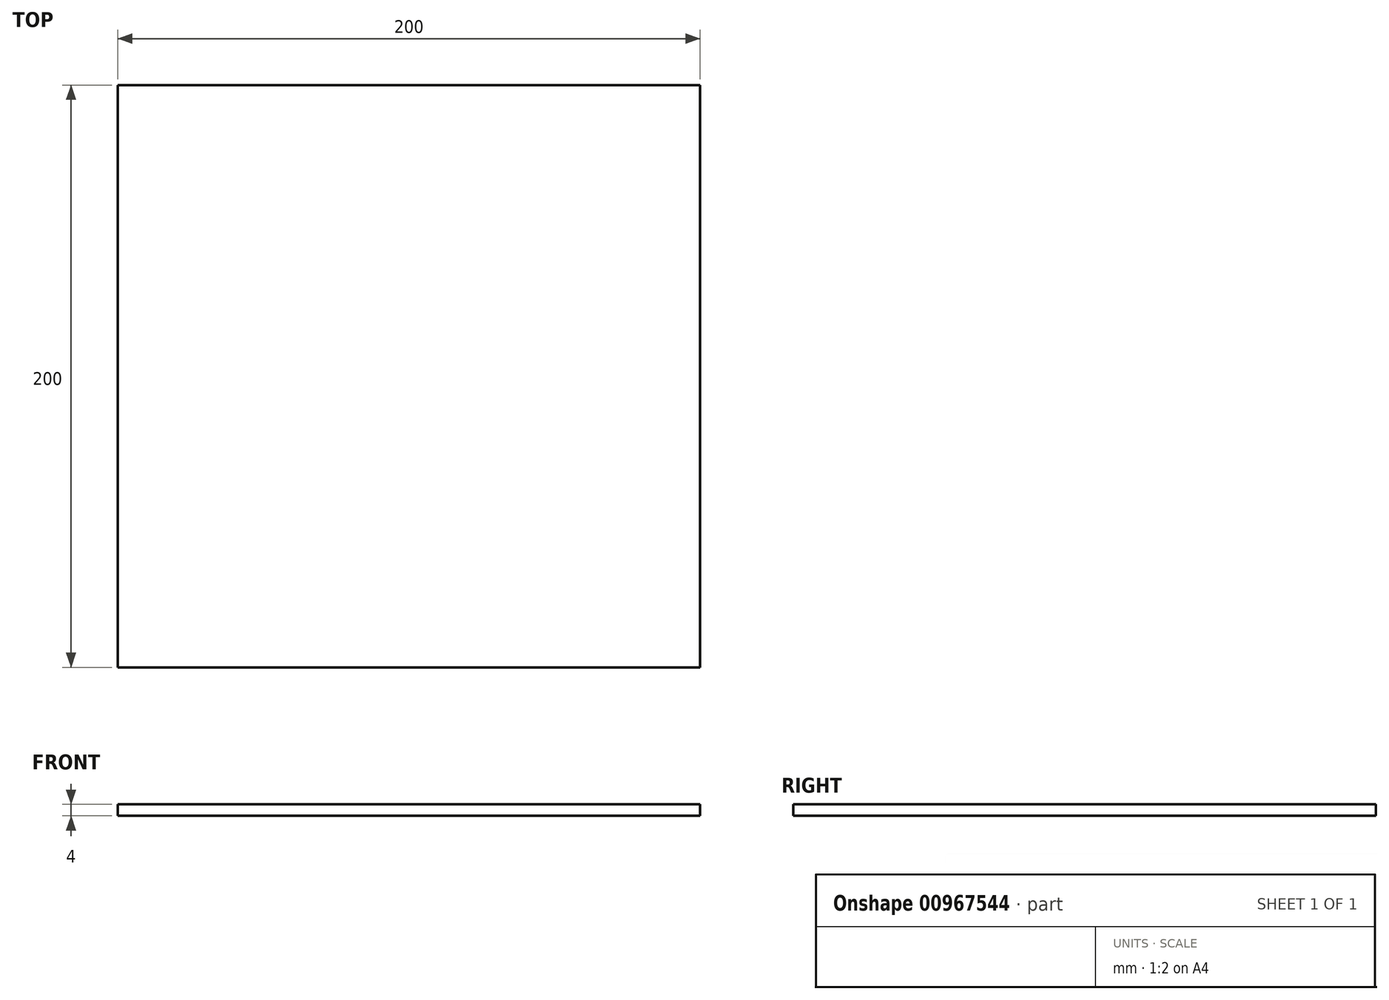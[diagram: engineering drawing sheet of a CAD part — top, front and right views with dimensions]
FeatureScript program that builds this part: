
annotation { "Feature Type Name" : "Feature", "Feature Type Description" : "" }
export const myFeature = defineFeature(function(context is Context, id is Id, definition is map)
    precondition{}
    {
        {
            var Q0;
            Q0=qCreatedBy(makeId("Top.planeOp"),FACE);
            var sketch = newSketch(context, id + "F0", { "sketchPlane" : qUnion([Q0])});
            skLineSegment(sketch, "E0.bottom", {"start": v(100, -100) * mm, "end": v(-100, -100) * mm});
            skLineSegment(sketch, "E0.top", {"start": v(100, 100) * mm, "end": v(-100, 100) * mm});
            skLineSegment(sketch, "E0.left", {"start": v(100, -100) * mm, "end": v(100, 100) * mm});
            skLineSegment(sketch, "E0.right", {"start": v(-100, -100) * mm, "end": v(-100, 100) * mm});
            skPoint(sketch, "E0.middle", {"position": v(0, 0) * mm});
            skSolve(sketch);
        }
        {
            var Q0;
            Q0=makeQuery(id+"F0.imprint","IMPRINT",FACE,{"disambiguationData":[TD([[makeQuery(id+"F0.imprint","IMPRINT",EDGE,{"derivedFrom":sQuery(id+"F0.wireOp",EDGE,"E0.bottom")}),-1.0]])]});
            extrude(context, id + "F1", {"entities" : qUnion([Q0]), "depth" : 4 * mm, "offsetDistance" : 25 * mm});
        }
    });
